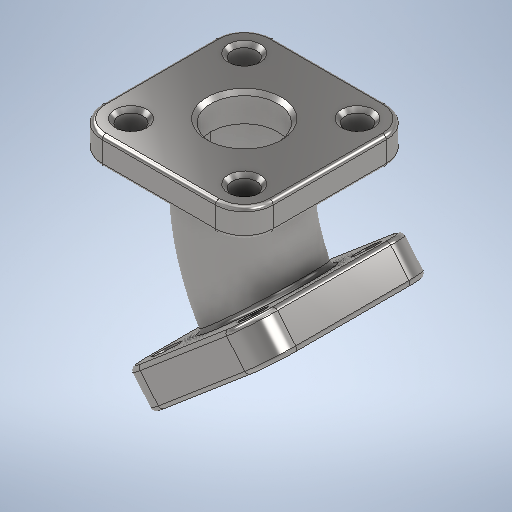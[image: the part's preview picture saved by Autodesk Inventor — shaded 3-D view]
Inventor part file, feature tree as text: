
AUTODESK INVENTOR PART (.ipt)
format: ipt  version: 2025.2 (Build 292293000, 293)  size: 548,864 bytes
history: native  units: in
note: dims shown in document units (in); Inventor stores cm internally (conversion verified against a paired STEP export)
features: sketch x6, extrude x2, fillet x2, sweep x1, chamfer x1
ambient origin geometry x8: Origin, YZ Plane, XZ Plane, XY Plane, X Axis, Y Axis, Z Axis, Center Point
bodies: Solid1 (feature_tree)
feature tree (12):
  sketch  "Sketch1"  dims[d3=8.8583in d7=3.4646in]
  sweep  "Sweep1"
  extrude  "Extrusion1"  TaperAngle=0.0deg  [1 undecoded]
  extrude  "Extrusion2"  Depth=8.8583in
  fillet  "Fillet1"  Radius=1.4961in
  fillet  "Fillet2"  Radius=1.2598in
  chamfer  "Chamfer1"  Distance=3.4646in
  sketch  "Sketch2"  dims[d11=8.8583in d12=8.8583in d13=1.4961in d14=1.2598in]
  sketch  "Sketch3"  dims[d15=1.2598in]
  sketch  "Sketch4"  dims[d16=1.2598in]
  sketch  "Sketch5"  dims[d17=1.2598in d18=3.4646in d19=1.4567in d20=0.0in d21=3.4646in d22=8.8583in d23=8.8583in d24=1.4961in d25=1.2598in d26=1.5748in d28=360.0deg d30=1.8504in d31=0.0in d32=0.1969in d33=0.1969in d34=0.1969in d35=0.0787in d36=45.0deg]
  sketch  "Sketch Circular Pattern1"  dims[d8=5.3937in d9=0.0in d10=0.0in]
note: 1 required parameter value undecoded (feature->parameter linkage not recoverable at this tier; creation-order binding heuristic only, values carry confidence <= 0.55)
